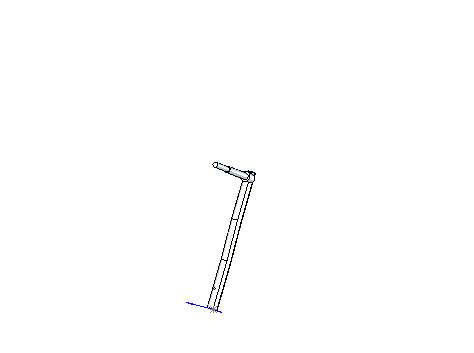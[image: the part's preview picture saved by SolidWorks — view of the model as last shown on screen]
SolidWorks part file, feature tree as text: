
SOLIDWORKS PART (.sldprt)
format: sldprt  version: not decoded by parser v0  size: 283,648 bytes
history: native  units: mm
features: plane x4, sketch x3, extrude x3, sweep x1, cut_extrude x1, chamfer x1, hole x1 + 7 further entries (+7 scaffold rows collapsed)
feature tree (28):
  scaffold x7  (default folders/planes/origin — collapsed)
  "Corps de surface"
  plane  "Face"
  plane  "Dessus"
  plane  "Droite"
  sketch  "Esquisse1"
  sketch  "param"  dims[c1.D1=25.0mm c1.D2=30.0mm c2.D1=30.0mm]
  "Esquisse2"
  sweep  "Balayage1"
  "Esquisse4"
  cut_extrude  "Enlèv. mat.-Extru.1"  [1 undecoded]
  chamfer  "Chanfrein1"  Distance=1.5mm Angle=45deg
  hole  "Diamètre du perçage M6.5 (6.500000)1"  [1 undecoded]
  sketch  "Esquisse3D1"  dims[D1=78.0mm D2=12.5mm]
  "Esquisse7"  4=25.4mm Diamètre du perçage=6.5mm Profondeur du perçage=32mm Angle de pointe=118deg
  plane  "Plan2"  Offset=58mm
  "Esquisse8"
  extrude  "Extrusion1"  Depth=40mm
  "Esquisse9"
  extrude  "Extrusion2"  Depth=150mm
  "Esquisse10"
  extrude  "Extrusion3"  Depth=100mm
decode coverage: 6 of 10 modeling features carry decoded parameters; 7 rows unclassified (native names shown)
note: 2 parameter values undecoded
note: suppression state not decoded; provenance and decode notes live in map.json
